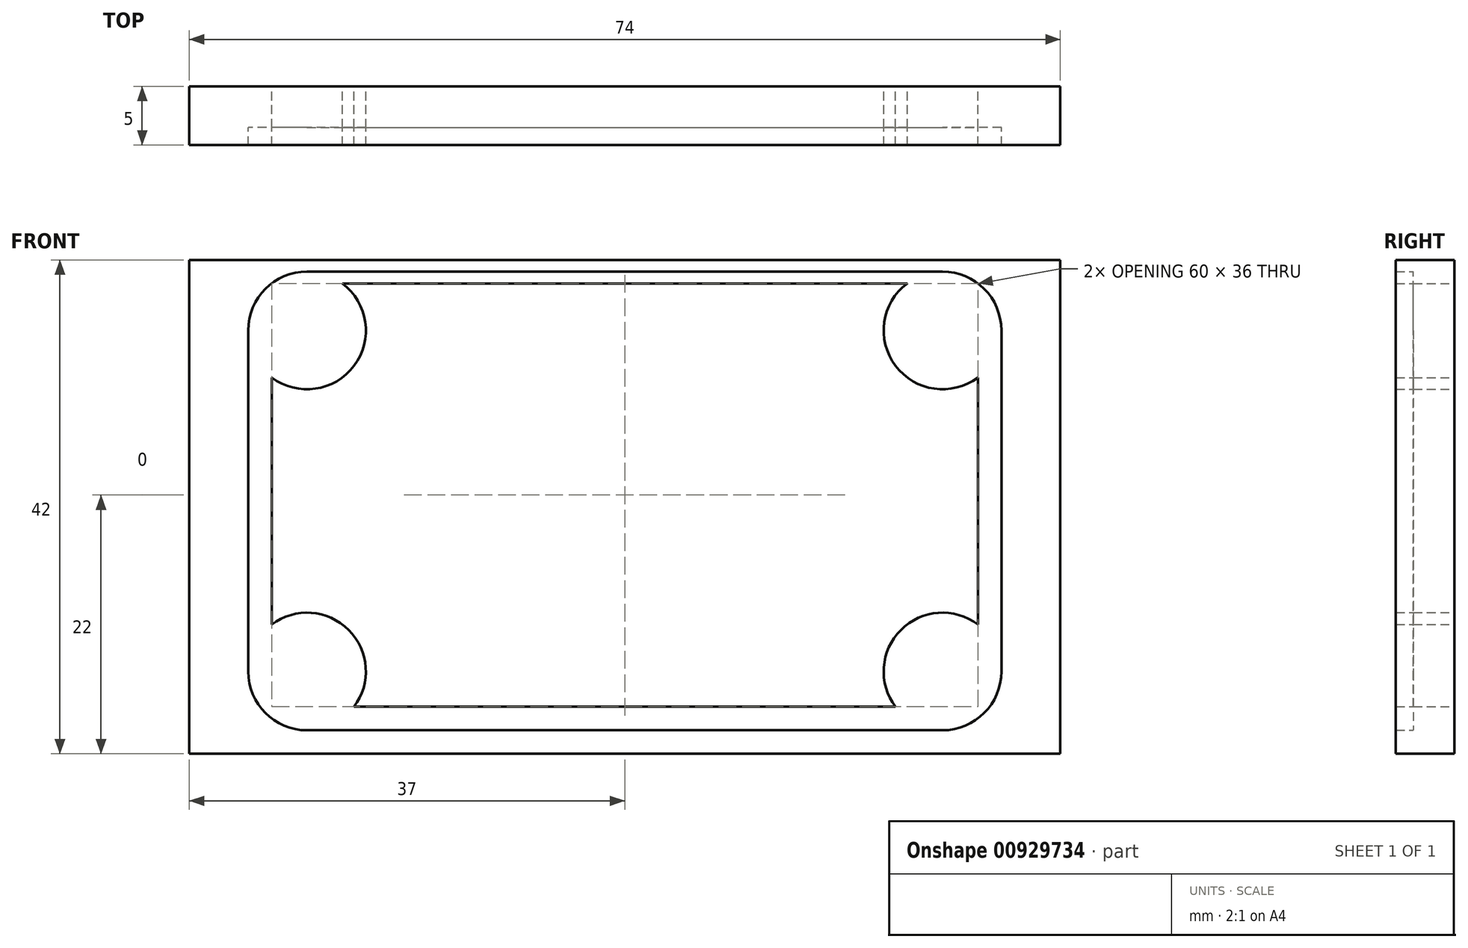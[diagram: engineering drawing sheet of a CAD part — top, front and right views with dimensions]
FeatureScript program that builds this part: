
annotation { "Feature Type Name" : "Feature", "Feature Type Description" : "" }
export const myFeature = defineFeature(function(context is Context, id is Id, definition is map)
    precondition{}
    {
        {
            var Q0;
            Q0=qCreatedBy(makeId("Front.planeOp"),FACE);
            var sketch = newSketch(context, id + "F0", { "sketchPlane" : qUnion([Q0])});
            skLineSegment(sketch, "E0.bottom", {"start": v(-32, 19.5) * mm, "end": v(32, 19.5) * mm});
            skLineSegment(sketch, "E0.top", {"start": v(-32, -19.5) * mm, "end": v(32, -19.5) * mm});
            skLineSegment(sketch, "E0.left", {"start": v(-32, 19.5) * mm, "end": v(-32, -19.5) * mm});
            skLineSegment(sketch, "E0.right", {"start": v(32, 19.5) * mm, "end": v(32, -19.5) * mm});
            skPoint(sketch, "E0.middle", {"position": v(0, 0) * mm});
            skArc(sketch, "E1", {"start": v(-30, 10.5) * mm, "mid": v(-23, 11.5) * mm, "end": v(-24, 18.5) * mm});
            skArc(sketch, "E2", {"start": v(30, -10.5) * mm, "mid": v(23.46, -10.96) * mm, "end": v(23, -17.5) * mm});
            skArc(sketch, "E3", {"start": v(-23, -17.5) * mm, "mid": v(-23.46, -10.96) * mm, "end": v(-30, -10.5) * mm});
            skLineSegment(sketch, "E4.bottom", {"start": v(-23, -17.5) * mm, "end": v(23, -17.5) * mm});
            skLineSegment(sketch, "E4.top", {"start": v(-24, 18.5) * mm, "end": v(24, 18.5) * mm});
            skLineSegment(sketch, "E4.left", {"start": v(-30, -10.5) * mm, "end": v(-30, 10.5) * mm});
            skLineSegment(sketch, "E4.right", {"start": v(30, -10.5) * mm, "end": v(30, 10.5) * mm});
            skArc(sketch, "E5", {"start": v(24, 18.5) * mm, "mid": v(23, 11.5) * mm, "end": v(30, 10.5) * mm});
            skLineSegment(sketch, "E6.bottom", {"start": v(-37, -21.5) * mm, "end": v(37, -21.5) * mm});
            skLineSegment(sketch, "E6.top", {"start": v(-37, 20.5) * mm, "end": v(37, 20.5) * mm});
            skLineSegment(sketch, "E6.left", {"start": v(-37, -21.5) * mm, "end": v(-37, 20.5) * mm});
            skLineSegment(sketch, "E6.right", {"start": v(37, -21.5) * mm, "end": v(37, 20.5) * mm});
            skSolve(sketch);
        }
        {
            var Q0;
            Q0=makeQuery(id+"F0.imprint","IMPRINT",FACE,{"disambiguationData":[TD([[makeQuery(id+"F0.imprint","IMPRINT",EDGE,{"derivedFrom":sQuery(id+"F0.wireOp",EDGE,"E0.bottom")}),1.0]])]});
            extrude(context, id + "F1", {"entities" : qUnion([Q0]), "depth" : 5 * mm, "offsetDistance" : 25 * mm});
        }
        {
            var Q0;
            Q0=makeQuery(id+"F0.imprint","IMPRINT",FACE,{"disambiguationData":[TD([[makeQuery(id+"F0.imprint","IMPRINT",EDGE,{"derivedFrom":sQuery(id+"F0.wireOp",EDGE,"E0.bottom")}),-1.0]])]});
            extrude(context, id + "F2", {"entities" : qUnion([Q0]), "operationType" : NewBodyOperationType.ADD, "depth" : 3.5 * mm, "offsetDistance" : 25 * mm});
        }
        {
            var Q0;
            Q0=makeQuery(id+"F1.opExtrude","SWEPT_EDGE",EDGE,{"disambiguationData":[OSD([sQuery(id+"F0.wireOp",EDGE,"E0.bottom"),sQuery(id+"F0.wireOp",EDGE,"E0.left")])]});
            var Q1;
            Q1=makeQuery(id+"F1.opExtrude","SWEPT_EDGE",EDGE,{"disambiguationData":[OSD([sQuery(id+"F0.wireOp",EDGE,"E0.top"),sQuery(id+"F0.wireOp",EDGE,"E0.left")])]});
            var Q2;
            Q2=makeQuery(id+"F1.opExtrude","SWEPT_EDGE",EDGE,{"disambiguationData":[OSD([sQuery(id+"F0.wireOp",EDGE,"E0.top"),sQuery(id+"F0.wireOp",EDGE,"E0.right")])]});
            var Q3;
            Q3=makeQuery(id+"F1.opExtrude","SWEPT_EDGE",EDGE,{"disambiguationData":[OSD([sQuery(id+"F0.wireOp",EDGE,"E0.bottom"),sQuery(id+"F0.wireOp",EDGE,"E0.right")])]});
            fillet(context, id + "F3", {"entities" : qUnion([Q0, Q1, Q2, Q3]), "radius" : 5 * mm, "tangentPropagation" : true, "allowEdgeOverflow" : false});
        }
        {
            var Q0;
            Q0=makeQuery(id+"F2.opExtrude","CAP_FACE",FACE,{"disambiguationData":[OSD([sQuery(id+"F0.wireOp",EDGE,"E0.bottom"),sQuery(id+"F0.wireOp",EDGE,"E0.top"),sQuery(id+"F0.wireOp",EDGE,"E0.left"),sQuery(id+"F0.wireOp",EDGE,"E0.right"),sQuery(id+"F0.wireOp",EDGE,"E1"),sQuery(id+"F0.wireOp",EDGE,"E2"),sQuery(id+"F0.wireOp",EDGE,"E3"),sQuery(id+"F0.wireOp",EDGE,"E4.bottom"),sQuery(id+"F0.wireOp",EDGE,"E4.top"),sQuery(id+"F0.wireOp",EDGE,"E4.left"),sQuery(id+"F0.wireOp",EDGE,"E4.right"),sQuery(id+"F0.wireOp",EDGE,"E5")])],"isStart":false});
            extrude(context, id + "F4", {"entities" : qUnion([Q0]), "depth" : 1.5 * mm, "offsetDistance" : 25 * mm});
        }
    });
